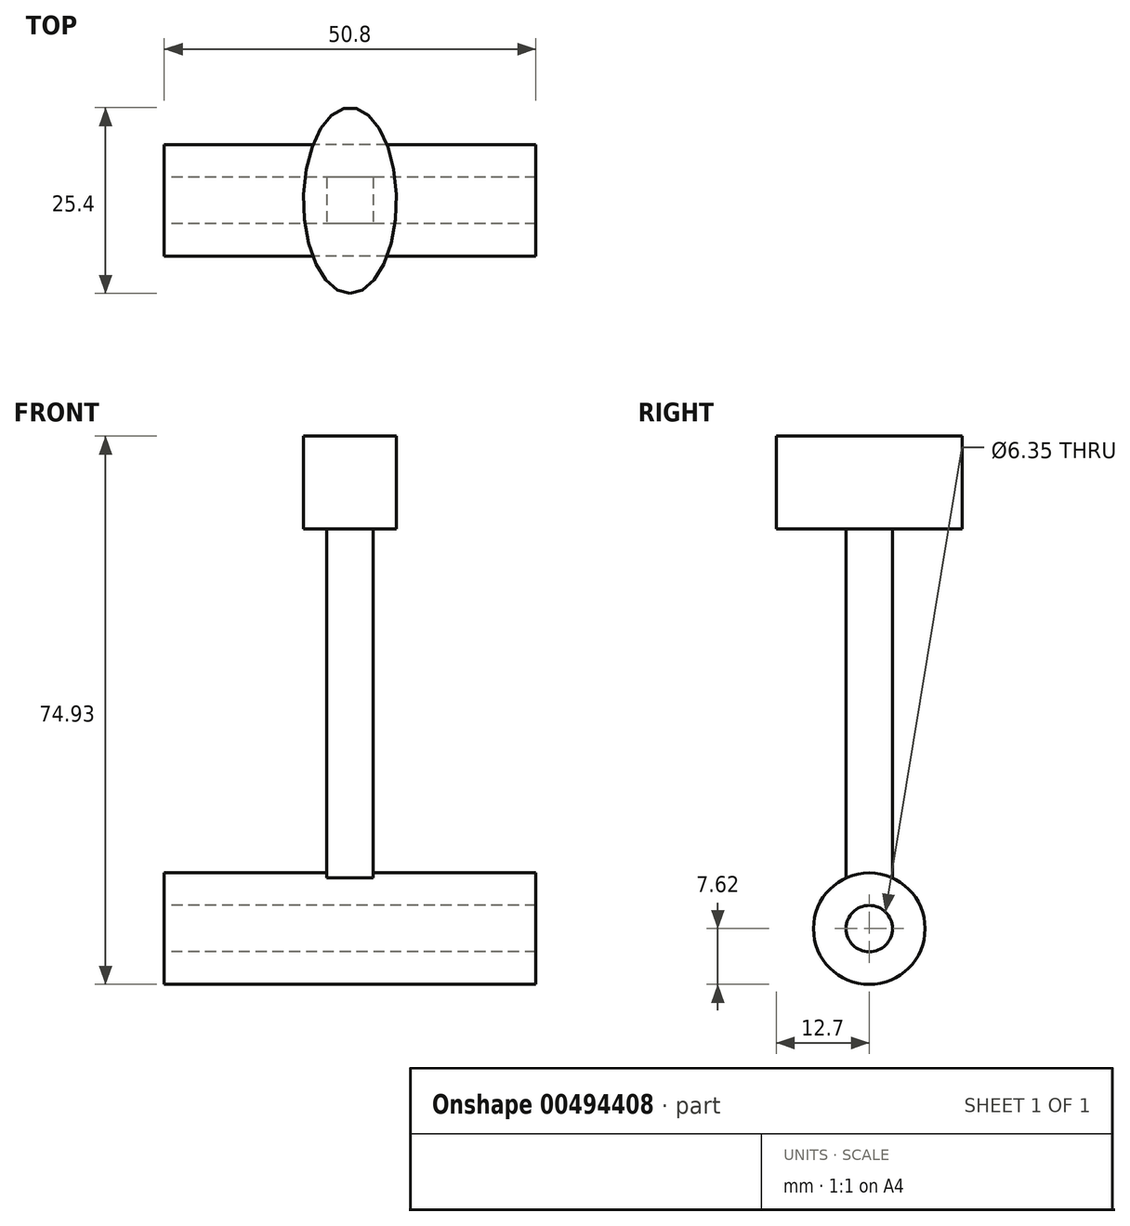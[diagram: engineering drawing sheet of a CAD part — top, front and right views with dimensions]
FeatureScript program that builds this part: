
annotation { "Feature Type Name" : "Feature", "Feature Type Description" : "" }
export const myFeature = defineFeature(function(context is Context, id is Id, definition is map)
    precondition{}
    {
        {
            var Q0;
            Q0=qCreatedBy(makeId("Right.planeOp"),FACE);
            var sketch = newSketch(context, id + "F0", { "sketchPlane" : qUnion([Q0])});
            skCircle(sketch, "E0", {"center": v(0, 0) * mm, "radius": 3.18 * mm});
            skCircle(sketch, "E1", {"center": v(0, 0) * mm, "radius": 7.62 * mm});
            skLineSegment(sketch, "E2", {"start": v(-3.18, 6.93) * mm, "end": v(-3.18, 67.31) * mm});
            skLineSegment(sketch, "E3", {"start": v(3.18, 6.93) * mm, "end": v(3.18, 67.31) * mm});
            skLineSegment(sketch, "E4", {"start": v(-3.18, 67.31) * mm, "end": v(3.18, 67.31) * mm});
            skSolve(sketch);
        }
        {
            var Q0;
            Q0=makeQuery(id+"F0.imprint","IMPRINT",FACE,{"disambiguationData":[TD([[makeQuery(id+"F0.imprint","IMPRINT",EDGE,{"derivedFrom":sQuery(id+"F0.wireOp",EDGE,"E0")}),-1.0]])]});
            extrude(context, id + "F1", {"entities" : qUnion([Q0]), "depth" : 50.8 * mm, "symmetric" : true});
        }
        {
            var Q0;
            {var subQ0=sQuery(id+"F0.wireOp",EDGE,"E2");Q0=makeQuery(id+"F0.imprint","IMPRINT",FACE,{"disambiguationData":[TD([[makeQuery(id+"F0.imprint","IMPRINT",EDGE,{"derivedFrom":subQ0}),-1.0]])]});}
            extrude(context, id + "F2", {"entities" : qUnion([Q0]), "operationType" : NewBodyOperationType.ADD, "depth" : 6.35 * mm, "symmetric" : true});
        }
        {
            var Q0;
            Q0=makeQuery(id+"F2.opExtrude","SWEPT_FACE",FACE,{"disambiguationData":[OSD([sQuery(id+"F0.wireOp",EDGE,"E4")])]});
            cPlane(context, id + "F3", {"entities" : qUnion([Q0]), "cplaneType" : CPlaneType.OFFSET, "offset" : 0 * mm, "width" : 152.4 * mm, "height" : 152.4 * mm});
        }
        {
            var Q0;
            Q0=qCreatedBy(id+"F3.planeOp",FACE);
            var sketch = newSketch(context, id + "F4", { "sketchPlane" : qUnion([Q0])});
            skEllipse(sketch, "E5", {"center": v(0, 0) * mm, "majorRadius": 12.7 * mm, "minorRadius": 6.35 * mm, "majorAxis": v(0, -1)});
            skSolve(sketch);
        }
        {
            var Q0;
            Q0=makeQuery(id+"F4.imprint","IMPRINT",FACE,{"disambiguationData":[TD([[makeQuery(id+"F4.imprint","IMPRINT",EDGE,{"derivedFrom":sQuery(id+"F4.wireOp",EDGE,"E5")}),1.0]])]});
            extrude(context, id + "F5", {"entities" : qUnion([Q0]), "operationType" : NewBodyOperationType.ADD, "oppositeDirection" : true, "depth" : 12.7 * mm});
        }
    });
